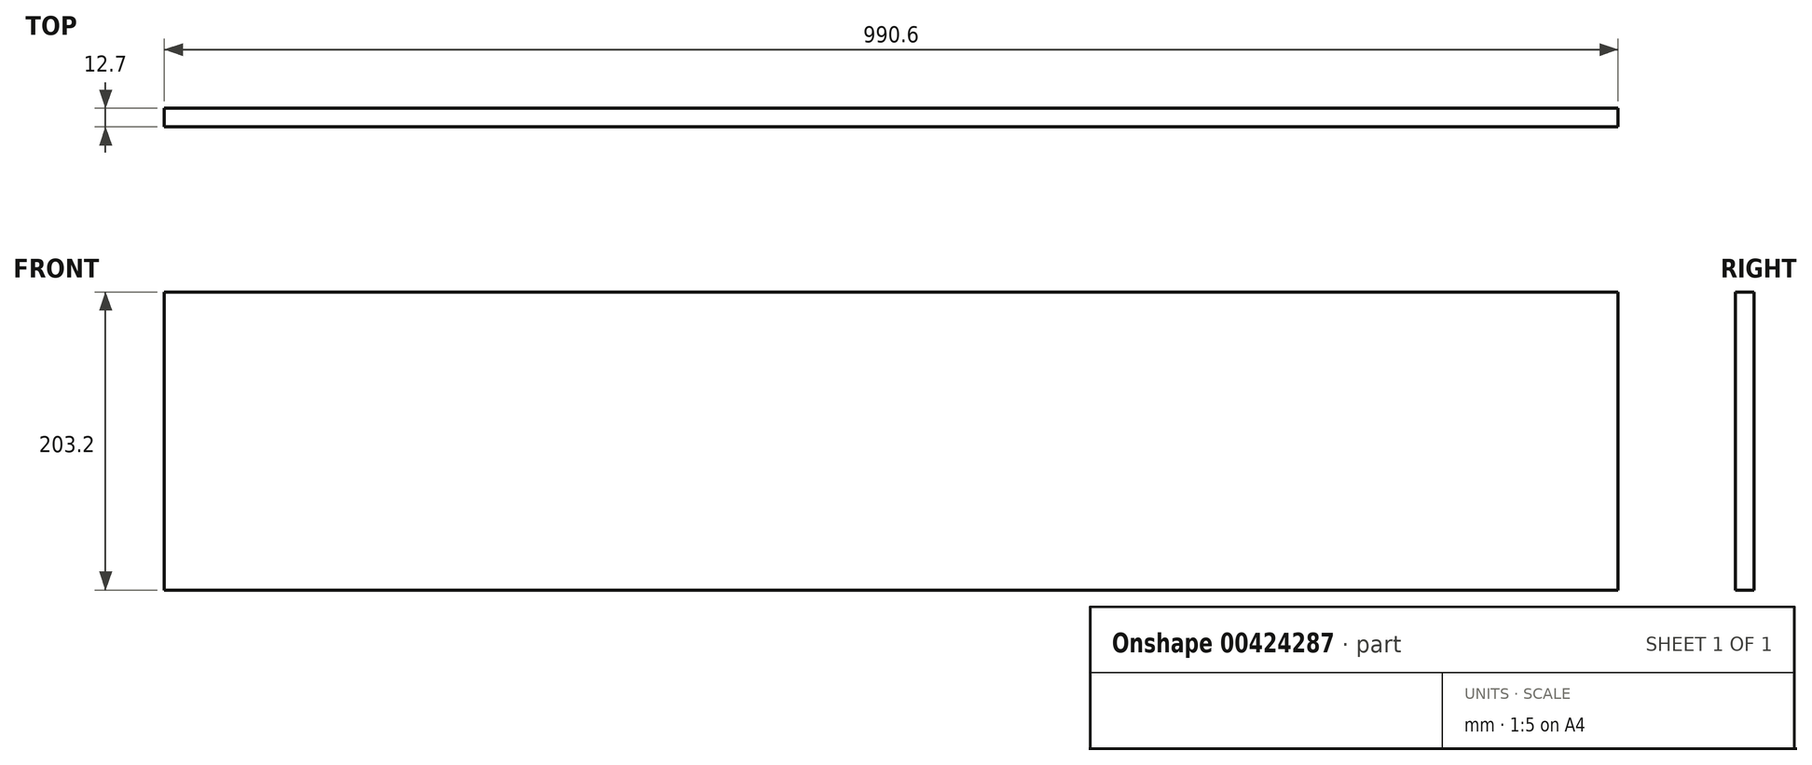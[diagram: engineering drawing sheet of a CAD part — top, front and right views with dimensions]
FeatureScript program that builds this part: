
annotation { "Feature Type Name" : "Feature", "Feature Type Description" : "" }
export const myFeature = defineFeature(function(context is Context, id is Id, definition is map)
    precondition{}
    {
        {
            var Q0;
            Q0=qCreatedBy(makeId("Front.planeOp"),FACE);
            var sketch = newSketch(context, id + "F0", { "sketchPlane" : qUnion([Q0])});
            skLineSegment(sketch, "E0.bottom", {"start": v(-876.83, 181.79) * mm, "end": v(113.77, 181.79) * mm});
            skLineSegment(sketch, "E0.top", {"start": v(-876.83, -21.41) * mm, "end": v(113.77, -21.41) * mm});
            skLineSegment(sketch, "E0.left", {"start": v(-876.83, 181.79) * mm, "end": v(-876.83, -21.41) * mm});
            skLineSegment(sketch, "E0.right", {"start": v(113.77, 181.79) * mm, "end": v(113.77, -21.41) * mm});
            skSolve(sketch);
        }
        {
            var Q0;
            Q0=makeQuery(id+"F0.imprint","IMPRINT",FACE,{"disambiguationData":[TD([[makeQuery(id+"F0.imprint","IMPRINT",EDGE,{"derivedFrom":sQuery(id+"F0.wireOp",EDGE,"E0.bottom")}),-1.0]])]});
            extrude(context, id + "F1", {"entities" : qUnion([Q0]), "depth" : 12.7 * mm});
        }
    });
